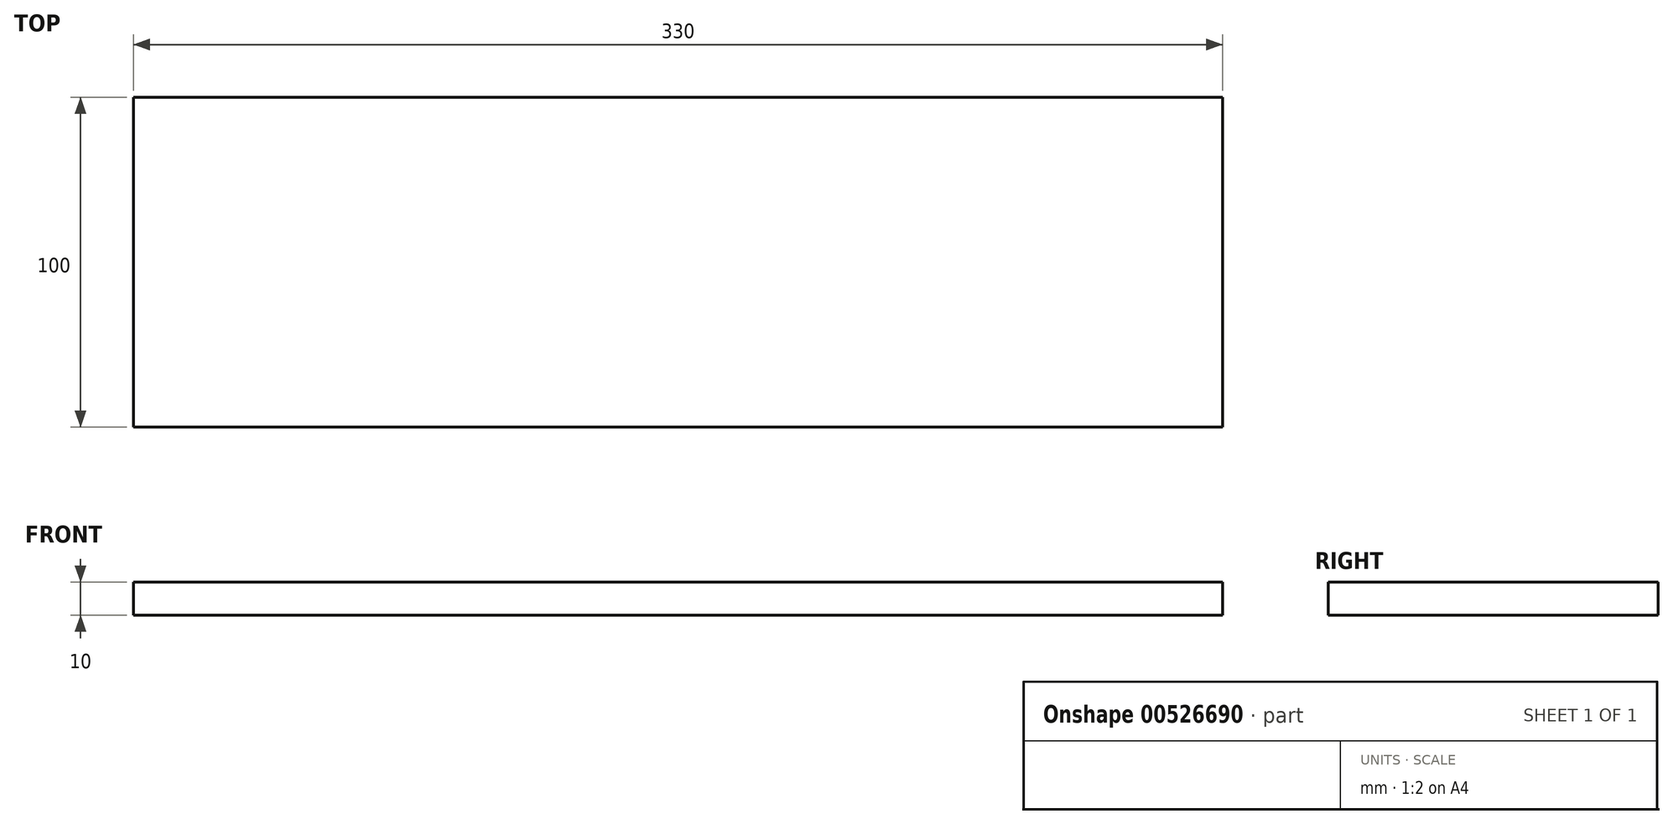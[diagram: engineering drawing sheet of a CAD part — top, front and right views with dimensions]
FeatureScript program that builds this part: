
annotation { "Feature Type Name" : "Feature", "Feature Type Description" : "" }
export const myFeature = defineFeature(function(context is Context, id is Id, definition is map)
    precondition{}
    {
        {
            var Q0;
            Q0=qCreatedBy(makeId("Top.planeOp"),FACE);
            var sketch = newSketch(context, id + "F0", { "sketchPlane" : qUnion([Q0])});
            skLineSegment(sketch, "E0.bottom", {"start": v(165, 50) * mm, "end": v(-165, 50) * mm});
            skLineSegment(sketch, "E0.top", {"start": v(165, -50) * mm, "end": v(-165, -50) * mm});
            skLineSegment(sketch, "E0.left", {"start": v(165, 50) * mm, "end": v(165, -50) * mm});
            skLineSegment(sketch, "E0.right", {"start": v(-165, 50) * mm, "end": v(-165, -50) * mm});
            skPoint(sketch, "E0.middle", {"position": v(0, 0) * mm});
            skSolve(sketch);
        }
        {
            var Q0;
            Q0 = qSketchRegion(id + "F0", true);
            extrude(context, id + "F1", {"entities" : qUnion([Q0]), "depth" : 10 * mm, "offsetDistance" : 25 * mm});
        }
    });
